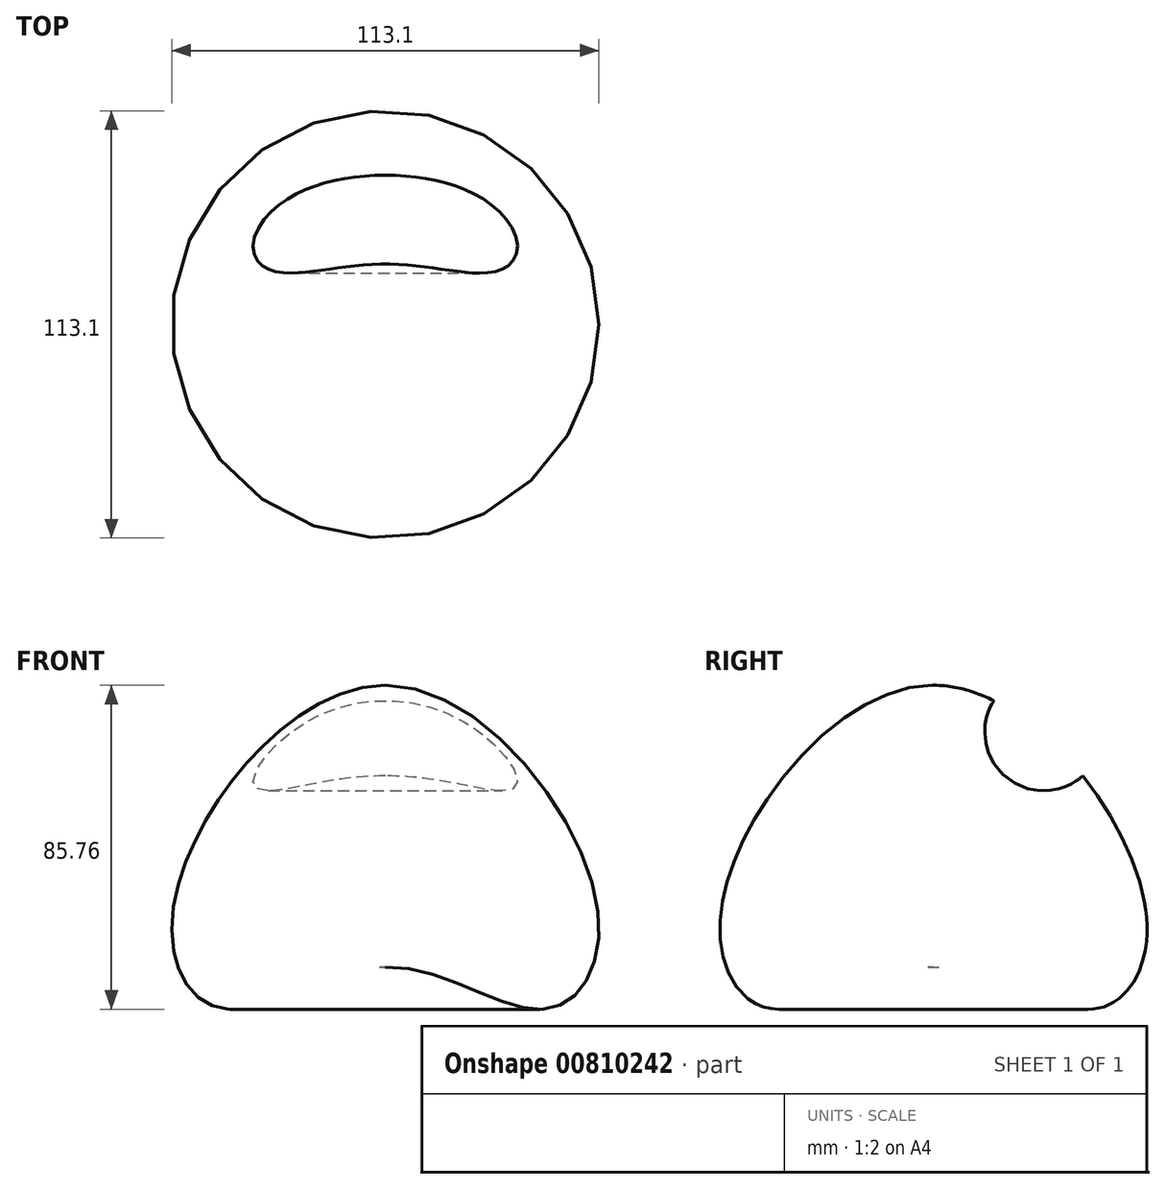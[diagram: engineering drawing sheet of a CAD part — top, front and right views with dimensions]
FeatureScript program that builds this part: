
annotation { "Feature Type Name" : "Feature", "Feature Type Description" : "" }
export const myFeature = defineFeature(function(context is Context, id is Id, definition is map)
    precondition{}
    {
        {
            var Q0;
            Q0=qCreatedBy(makeId("Front.planeOp"),FACE);
            var sketch = newSketch(context, id + "F0", { "sketchPlane" : qUnion([Q0])});
            skFitSpline(sketch, "E0", {"points": [v(0, 58.27) * mm, v(56.05, 0) * mm, v(42.61, -27.4) * mm, v(0, -16.39) * mm, v(-37.66, -30.2) * mm, v(-51.9, 0) * mm, v(0, 58.27) * mm]});
            skLineSegment(sketch, "E1", {"start": v(0, 58.27) * mm, "end": v(0, -16.39) * mm});
            skSolve(sketch);
        }
        {
            var Q0;
            {var subQ0=sQuery(id+"F0.wireOp",EDGE,"E1");Q0=makeQuery(id+"F0.imprint","IMPRINT",FACE,{"disambiguationData":[TD([[makeQuery(id+"F0.imprint","IMPRINT",EDGE,{"derivedFrom":subQ0}),1.0]])]});}
            var Q1;
            Q1=sQuery(id+"F0.wireOp",EDGE,"E1");
            revolve(context, id + "F1", {"surfaceOperationType" : NewSurfaceOperationType.NEW, "entities" : qUnion([Q0]), "axis" : qUnion([Q1]), "revolveType" : RevolveType.FULL});
        }
        {
            var Q0;
            Q0=qCreatedBy(makeId("Right.planeOp"),FACE);
            var sketch = newSketch(context, id + "F2", { "sketchPlane" : qUnion([Q0])});
            skCircle(sketch, "E2", {"center": v(29.15, 45.91) * mm, "radius": 15.56 * mm});
            skSolve(sketch);
        }
        {
            var Q0;
            Q0=makeQuery(id+"F2.imprint","IMPRINT",FACE,{"disambiguationData":[TD([[makeQuery(id+"F2.imprint","IMPRINT",EDGE,{"derivedFrom":sQuery(id+"F2.wireOp",EDGE,"E2")}),1.0]])]});
            var Q1;
            Q1=sQuery(id+"F2.wireOp",EDGE,"E2");
            extrude(context, id + "F3", {"entities" : qUnion([Q0]), "operationType" : NewBodyOperationType.REMOVE, "surfaceEntities" : qUnion([Q1]), "oppositeDirection" : true, "depth" : 200 * mm, "offsetDistance" : 25 * mm});
        }
        {
            var Q0;
            Q0=makeQuery(id+"F2.imprint","IMPRINT",FACE,{"disambiguationData":[TD([[makeQuery(id+"F2.imprint","IMPRINT",EDGE,{"derivedFrom":sQuery(id+"F2.wireOp",EDGE,"E2")}),1.0]])]});
            extrude(context, id + "F4", {"entities" : qUnion([Q0]), "operationType" : NewBodyOperationType.REMOVE, "depth" : 200 * mm, "offsetDistance" : 25 * mm});
        }
    });
